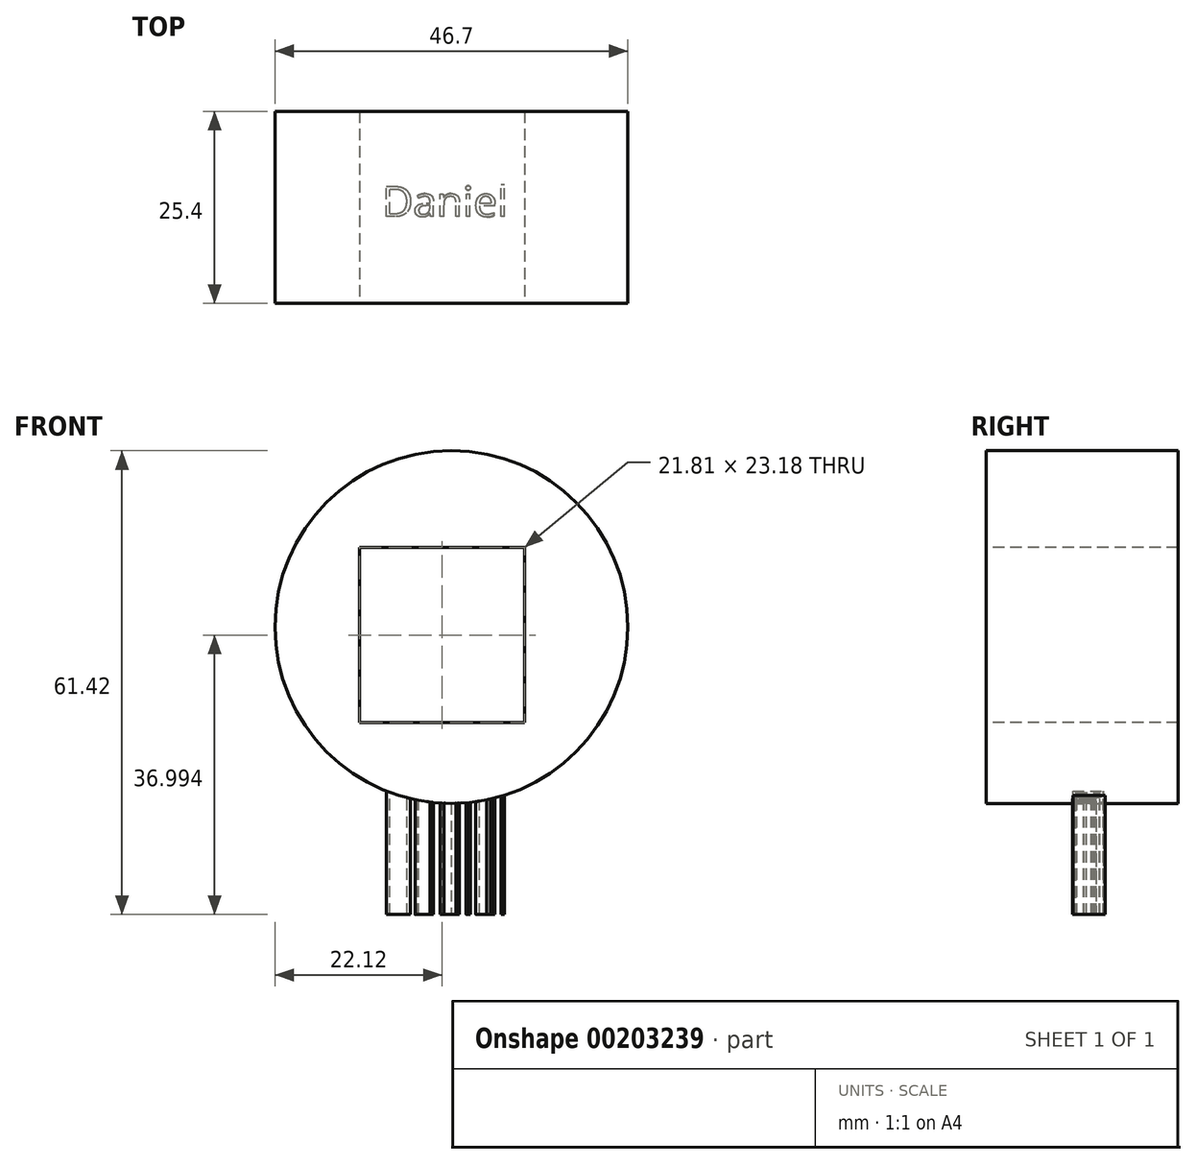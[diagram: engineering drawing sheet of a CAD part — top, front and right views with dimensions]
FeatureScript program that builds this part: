
annotation { "Feature Type Name" : "Feature", "Feature Type Description" : "" }
export const myFeature = defineFeature(function(context is Context, id is Id, definition is map)
    precondition{}
    {
        {
            var Q0;
            Q0=qCreatedBy(makeId("Front.planeOp"),FACE);
            var sketch = newSketch(context, id + "F0", { "sketchPlane" : qUnion([Q0])});
            skCircle(sketch, "E0", {"center": v(0, 0) * mm, "radius": 23.35 * mm});
            skSolve(sketch);
        }
        {
            var Q0;
            Q0 = qSketchRegion(id + "F0", true);
            extrude(context, id + "F1", {"entities" : qUnion([Q0]), "depth" : 25.4 * mm});
        }
        {
            var Q0;
            Q0=makeQuery(id+"F1.opExtrude","CAP_FACE",FACE,{"disambiguationData":[OSD([sQuery(id+"F0.wireOp",EDGE,"E0")])],"isStart":false});
            var sketch = newSketch(context, id + "F2", { "sketchPlane" : qUnion([Q0])});
            skLineSegment(sketch, "E1.bottom", {"start": v(-12.13, 10.52) * mm, "end": v(9.67, 10.52) * mm});
            skLineSegment(sketch, "E1.top", {"start": v(-12.13, -12.67) * mm, "end": v(9.67, -12.67) * mm});
            skLineSegment(sketch, "E1.left", {"start": v(-12.13, 10.52) * mm, "end": v(-12.13, -12.67) * mm});
            skLineSegment(sketch, "E1.right", {"start": v(9.67, 10.52) * mm, "end": v(9.67, -12.67) * mm});
            skSolve(sketch);
        }
        {
            var Q0;
            Q0 = qSketchRegion(id + "F2", true);
            extrude(context, id + "F3", {"entities" : qUnion([Q0]), "operationType" : NewBodyOperationType.REMOVE, "oppositeDirection" : true, "depth" : 25.4 * mm});
        }
        {
            var Q0;
            Q0=makeQuery(id+"F3.boolean.opBoolean","COPY",FACE,{"derivedFrom":makeQuery(id+"F3.opExtrude","SWEPT_FACE",FACE,{"disambiguationData":[OSD([sQuery(id+"F2.wireOp",EDGE,"E1.top")])]})});
            var sketch = newSketch(context, id + "F4", { "sketchPlane" : qUnion([Q0])});
            skText(sketch, "E2", { "text": "Daniel", "fontName": "OpenSans-Regular.ttf"});
            const initialGuessF4  = {"E2": [-0.00915, -0.01393, 1, 0, 0.00404]};
            skSetInitialGuess(sketch, initialGuessF4);
            skSolve(sketch);
        }
        {
            var Q0;
            Q0 = qSketchRegion(id + "F4", true);
            extrude(context, id + "F5", {"entities" : qUnion([Q0]), "operationType" : NewBodyOperationType.ADD, "oppositeDirection" : true, "depth" : 25.4 * mm});
        }
    });
